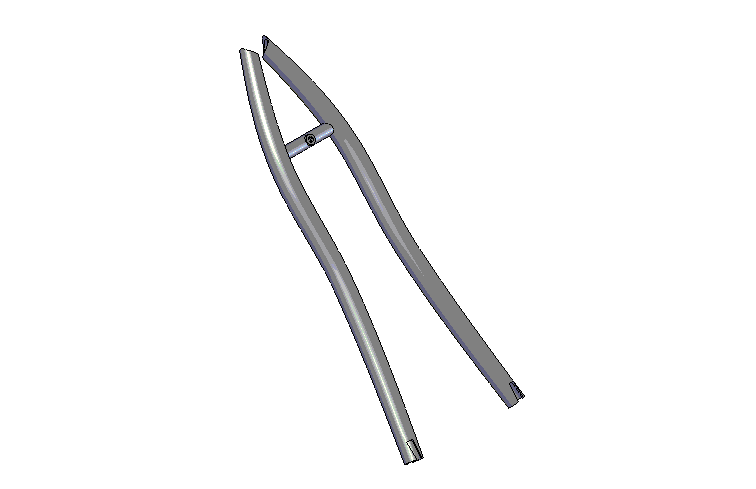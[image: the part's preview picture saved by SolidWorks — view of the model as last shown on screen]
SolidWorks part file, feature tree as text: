
SOLIDWORKS PART (.sldprt)
format: sldprt  version: not decoded by parser v0  size: 2,588,672 bytes
history: native  units: mm
features: plane x16, sketch x16, cut_extrude x5, shell x2, extrude x2, material x1, mirror x1 (+10 scaffold rows collapsed)
feature tree (53):
  scaffold x10  (default folders/planes/origin — collapsed)
  material  "Matériau <non spécifié>"
  plane  "Plan de face"
  plane  "Plan de dessus"
  plane  "Plan de droite"
  sketch  "Esquisse1"  dims[c1.D13=30.0mm c1.D1=625.0mm c1.D2=460.0mm c1.D3=545.0mm c1.D4=27.0mm c1.D5=500.0mm c1.D6=445.0mm c1.D7=670.0mm c2.D1=622.0mm c2.D2=670.0mm c2.D3=545.0mm c2.D4=460.0mm c2.D5=445.0mm c2.D6=495.0mm c2.D7=535.0mm c2.D8=27.0mm c2.D9=8.0mm c2.D10=155.0mm c2.D11=400.0mm c2.D12=~545.374305mm c3.D12=56.0deg]
  plane  "Plan1"
  plane  "Plan6"
  plane  "Plan7"  Offset=500mm
  plane  "Plan8"  Offset=287mm
  sketch  "Esquisse13"  dims[c1.D1=150.0mm c1.D2=250.0mm c1.D5=200.0mm c1.D7=150.0mm c1.D3=450.0mm c1.D4=~221.56758mm c2.D5=110.0mm c2.D6=~61.253667mm c2.D7=87.0mm c2.D8=95.0mm c2.D4=145.0mm c2.D9=13.0mm c3.D5=87.0mm c3.D6=260.0mm]
  plane  "Plan9"
  plane  "Plan10"
  plane  "Plan11"
  plane  "Plan12"
  plane  "Plan13"
  plane  "Plan14"
  sketch  "Esquisse14"  dims[D1=17.0mm]
  sketch  "Esquisse15"  dims[D1=22.0mm]
  sketch  "Esquisse16"  dims[D1=22.5mm]
  sketch  "Esquisse17"  dims[D1=22.0mm]
  sketch  "Esquisse18"  dims[D1=22.0mm]
  sketch  "Esquisse19"  dims[c1.D1=17.0mm c1.D2=17.0mm c2.D1=20.0mm]
  mirror  "Symétrie2"
  sketch  "Esquisse2"  dims[D1=32.0mm D2=28.0mm]
  cut_extrude  "Enlèv. mat.-Extru.2"  [1 undecoded]
  shell  "Coque3"  Thickness=2mm
  shell  "Coque4"  Thickness=2mm
  sketch  "Esquisse22"  dims[D1=14.0mm D2=10.0mm D3=113.5mm]
  extrude  "Extrusion3"  [1 undecoded]
  sketch  "Esquisse23"  dims[D1=10.0mm]
  cut_extrude  "Enlèv. mat.-Extru.3"  [1 undecoded]
  plane  "Plan15"  Offset=71.75mm
  sketch  "Esquisse24"  dims[c1.D1=10.0mm c1.D2=15.0mm c1.D3=19.0mm c1.D5=6.0mm c1.D6=6.0mm c1.D8=~13.175347mm c1.D15=12.0mm c1.D18=6.0mm c1.D19=16.0mm c1.D20=44.0mm c2.D6=8.0mm c2.D19=8.0mm c2.D22=19.0mm c3.D19=13.0mm c3.D23=8.0mm c3.D24=30.0mm c3.D1=~23.333356mm c3.D4=460.0mm c4.D4=~76.317285deg c5.D4=~104.669232mm c6.D4=~118.797025deg c7.D4=460.0mm c8.D4=72.0deg c8.D7=40.0mm c8.D8=23.0mm c8.D9=30.0mm c8.D10=60.0mm c8.D11=7.0mm c8.D12=13.0mm c8.D13=24.0mm c8.D14=70.0mm c8.D16=78.0mm c8.D17=78.0mm c8.D18=78.0mm c9.D17=78.0mm c9.D16=78.0mm c10.D17=34.0mm c10.D21=10.0mm c10.D18=51.0mm c10.D19=12.0mm c10.D22=20.0mm c10.D23=20.0mm c11.D22=20.0mm c11.D23=12.0mm c12.D22=20.0mm c12.D23=20.0mm c13.D22=20.0mm c13.D23=20.0mm c14.D22=20.0mm c14.D23=20.0mm c15.D22=20.0mm c15.D23=20.0mm c15.D19=12.0mm c16.D22=21.5mm c16.D23=28.0mm c16.D2=70.0mm]
  plane  "Plan16"  Offset=143.5mm
  cut_extrude  "Enlèv. mat.-Extru.6"  Depth=7mm
  sketch  "Esquisse27"  dims[c1.D1=44.0mm c1.D3=3.0mm c2.D1=22.0mm c2.D2=8.0mm c2.D4=11.0mm c2.D5=70.0mm c3.D1=70.0mm]
  cut_extrude  "Enlèv. mat.-Extru.5"  Depth=4.25mm
  sketch  "Esquisse28"
  plane  "Plan18"
  sketch  "Esquisse29"  dims[D1=11.0mm D2=6.0mm]
  extrude  "Extrusion4"  [1 undecoded]
  sketch  "Esquisse30"  dims[D1=4.2mm D2=4.2mm]
  cut_extrude  "Enlèv. mat.-Extru.7"  [1 undecoded]
decode coverage: 19 of 26 modeling features carry decoded parameters
note: ~ marks probable driven/reference dimensions
note: 5 parameter values undecoded
summary: no parameter record found for 5 features
note: suppression state not decoded; provenance and decode notes live in map.json
